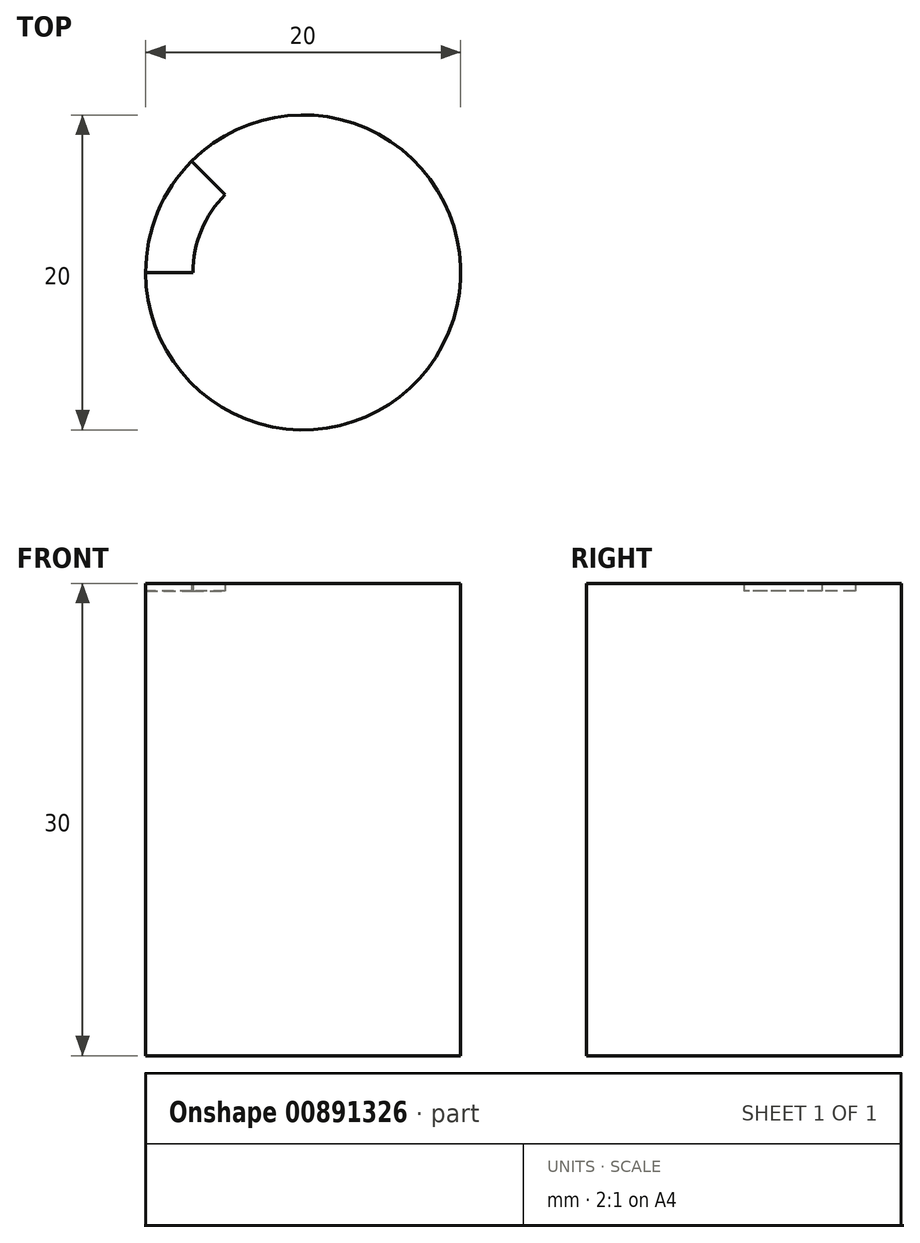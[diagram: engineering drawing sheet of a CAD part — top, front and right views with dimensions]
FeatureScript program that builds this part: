
annotation { "Feature Type Name" : "Feature", "Feature Type Description" : "" }
export const myFeature = defineFeature(function(context is Context, id is Id, definition is map)
    precondition{}
    {
        {
            var Q0;
            Q0=qCreatedBy(makeId("Top.planeOp"),FACE);
            var sketch = newSketch(context, id + "F0", { "sketchPlane" : qUnion([Q0])});
            skCircle(sketch, "E0", {"center": v(0, 0) * mm, "radius": 10 * mm});
            skSolve(sketch);
        }
        {
            var Q0;
            Q0 = qSketchRegion(id + "F0", true);
            extrude(context, id + "F1", {"entities" : qUnion([Q0]), "depth" : 30 * mm, "offsetDistance" : 25 * mm});
        }
        {
            var Q0;
            Q0=qCreatedBy(makeId("Front.planeOp"),FACE);
            var sketch = newSketch(context, id + "F2", { "sketchPlane" : qUnion([Q0])});
            skLineSegment(sketch, "E1.0", {"start": v(-10, 30) * mm, "end": v(10, 30) * mm});
            skLineSegment(sketch, "E2.bottom", {"start": v(-10, 30) * mm, "end": v(-7, 30) * mm});
            skLineSegment(sketch, "E2.top", {"start": v(-10, 29.5) * mm, "end": v(-7, 29.5) * mm});
            skLineSegment(sketch, "E2.left", {"start": v(-10, 30) * mm, "end": v(-10, 29.5) * mm});
            skLineSegment(sketch, "E2.right", {"start": v(-7, 30) * mm, "end": v(-7, 29.5) * mm});
            skLineSegment(sketch, "E3", {"start": v(0, 0) * mm, "end": v(0, 60.6) * mm});
            skSolve(sketch);
        }
        {
            var Q0;
            Q0=makeQuery(id+"F2.imprint","IMPRINT",FACE,{"disambiguationData":[TD([[makeQuery(id+"F2.imprint","IMPRINT",EDGE,{"derivedFrom":sQuery(id+"F2.wireOp",EDGE,"E2.top")}),1.0]])]});
            var Q1;
            Q1=sQuery(id+"F2.wireOp",EDGE,"E3");
            revolve(context, id + "F3", {"operationType" : NewBodyOperationType.REMOVE, "surfaceOperationType" : NewSurfaceOperationType.NEW, "entities" : qUnion([Q0]), "axis" : qUnion([Q1]), "revolveType" : RevolveType.ONE_DIRECTION, "oppositeDirection" : true, "angle" : 45 * degree});
        }
    });
